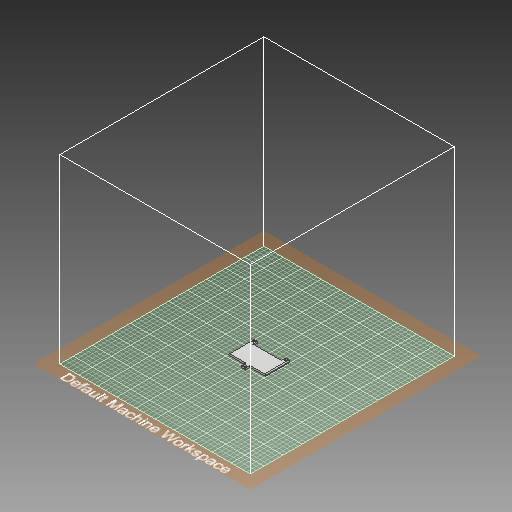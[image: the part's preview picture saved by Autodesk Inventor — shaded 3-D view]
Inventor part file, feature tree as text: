
AUTODESK INVENTOR PART (.ipt)
format: ipt  version: 2019.4 (Build 234330000, 330)  size: 374,272 bytes
history: native  units: in
note: dims shown in document units (in); Inventor stores cm internally (conversion verified against a paired STEP export)
features: sketch x4, extrude x3, fillet x1
ambient origin geometry x8: Origin, YZ Plane, XZ Plane, XY Plane, X Axis, Y Axis, Z Axis, Center Point
bodies: Solid1 (feature_tree)
feature tree (8):
  extrude  "Extrusion1"  Depth=1.7717in
  sketch  "Sketch2"  dims[d2=0.3937in d3=0.3937in]
  extrude  "Extrusion2"  Depth=0.3937in
  extrude  "Extrusion3"  Depth=0.3937in
  fillet  "Fillet2"  Radius=1.4878in
  sketch  "Sketch1"  dims[d0=3.2283in d1=1.7717in]
  sketch  "Sketch3"  dims[d4=0.3937in d5=0.3937in d10=1.4878in]
  sketch  "Sketch4"  dims[d11=0.3937in d12=0.3937in d15=0.126in d16=0.2362in d20=0.126in d21=0.126in d22=0.1575in d23=0.0in d24=0.2165in d25=0.2165in d26=0.2165in d27=0.0984in d28=0.0in d30=0.0197in d31=0.0197in d32=0.0197in d33=0.0197in d34=0.0197in d35=0.0197in d36=0.0197in d37=0.0197in d38=0.0197in d39=0.0197in d40=0.0197in d41=0.3937in d42=0.0in d43=0.0787in]
